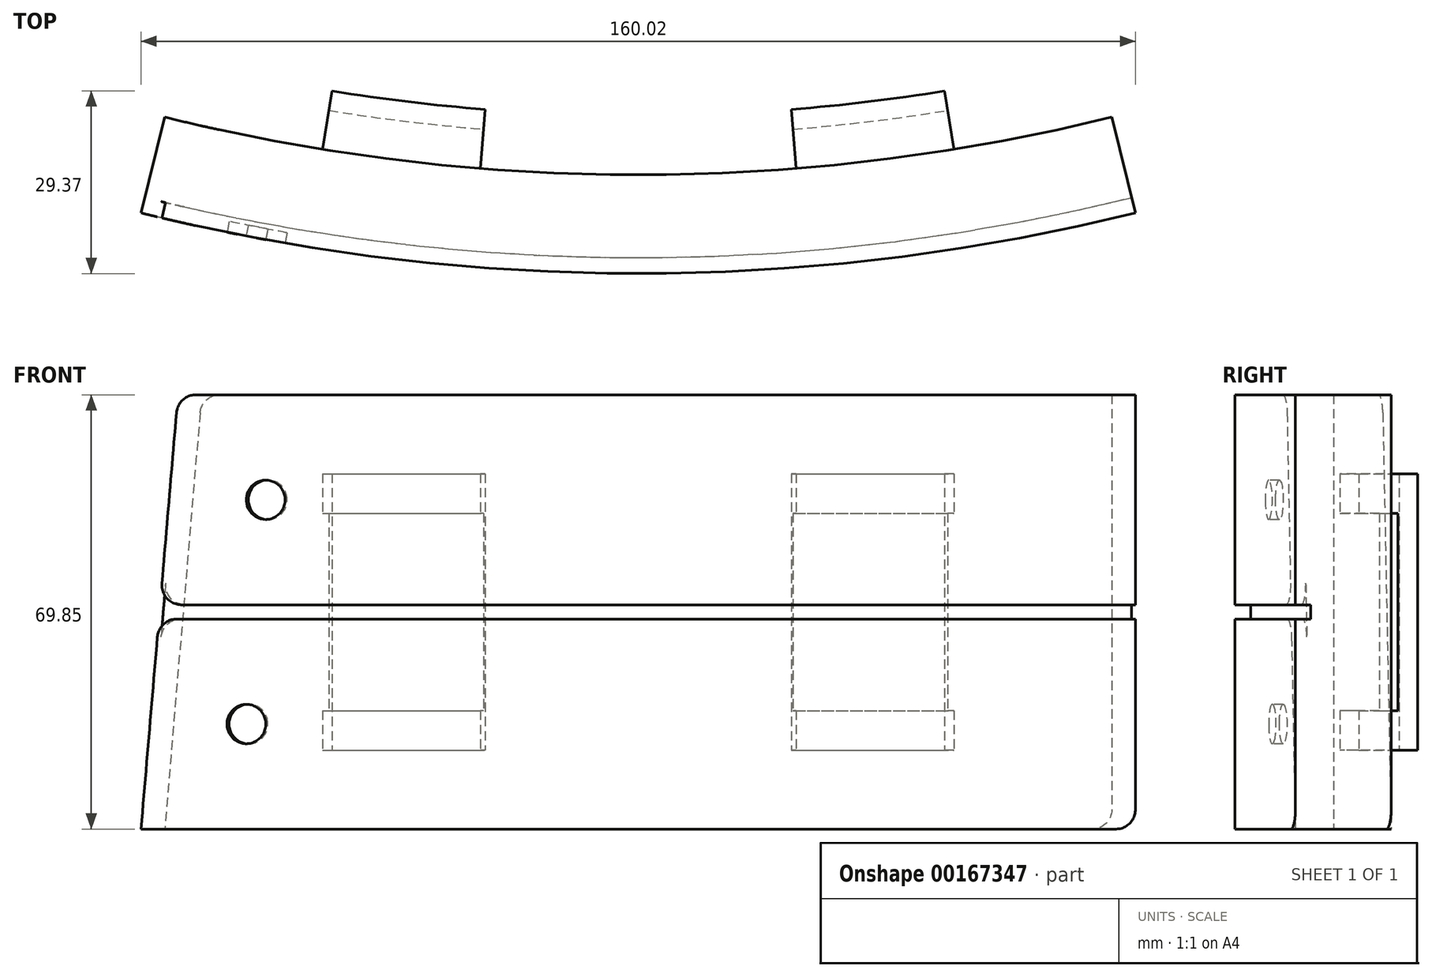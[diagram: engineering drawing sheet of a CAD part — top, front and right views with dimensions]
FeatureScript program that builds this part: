
annotation { "Feature Type Name" : "Feature", "Feature Type Description" : "" }
export const myFeature = defineFeature(function(context is Context, id is Id, definition is map)
    precondition{}
    {
        {
            var Q0;
            Q0=qCreatedBy(makeId("Top.planeOp"),FACE);
            var sketch = newSketch(context, id + "F0", { "sketchPlane" : qUnion([Q0])});
            skLineSegment(sketch, "E0.bottom", {"start": v(76.2, -22.11) * mm, "end": v(-76.2, -22.11) * mm, "construction": true});
            skLineSegment(sketch, "E0.top", {"start": v(76.2, 22.11) * mm, "end": v(-76.2, 22.11) * mm, "construction": true});
            skLineSegment(sketch, "E0.left", {"start": v(76.2, -22.11) * mm, "end": v(76.2, 22.11) * mm, "construction": true});
            skLineSegment(sketch, "E0.right", {"start": v(-76.2, -22.11) * mm, "end": v(-76.2, 22.11) * mm, "construction": true});
            skPoint(sketch, "E0.middle", {"position": v(0, 0) * mm});
            skLineSegment(sketch, "E1", {"start": v(0, 0) * mm, "end": v(0, 381.3) * mm, "construction": true});
            skArc(sketch, "E2", {"start": v(-76.2, -22.11) * mm, "mid": v(0, -31.4) * mm, "end": v(76.2, -22.11) * mm});
            skLineSegment(sketch, "E3", {"start": v(-76.2, -22.11) * mm, "end": v(0, 286.1) * mm, "construction": true});
            skLineSegment(sketch, "E4", {"start": v(76.2, -22.11) * mm, "end": v(0, 286.1) * mm, "construction": true});
            skArc(sketch, "E5", {"start": v(-80, -37.52) * mm, "mid": v(0, -47.27) * mm, "end": v(80, -37.52) * mm});
            skLineSegment(sketch, "E6", {"start": v(-76.2, -22.11) * mm, "end": v(-80, -37.52) * mm});
            skLineSegment(sketch, "E7", {"start": v(76.2, -22.11) * mm, "end": v(80, -37.52) * mm});
            skArc(sketch, "E8", {"start": v(-79.4, -35.06) * mm, "mid": v(0, -44.73) * mm, "end": v(79.4, -35.06) * mm});
            skSolve(sketch);
        }
        {
            var Q0;
            {var subQ0=sQuery(id+"F0.wireOp",EDGE,"E2");Q0=makeQuery(id+"F0.imprint","IMPRINT",FACE,{"disambiguationData":[TD([[makeQuery(id+"F0.imprint","IMPRINT",EDGE,{"derivedFrom":subQ0}),-1.0]])]});}
            var Q1;
            {var subQ0=sQuery(id+"F0.wireOp",EDGE,"E5");Q1=makeQuery(id+"F0.imprint","IMPRINT",FACE,{"disambiguationData":[TD([[makeQuery(id+"F0.imprint","IMPRINT",EDGE,{"derivedFrom":subQ0}),1.0]])]});}
            extrude(context, id + "F1", {"entities" : qUnion([Q0, Q1]), "depth" : 69.85 * mm});
        }
        {
            var Q0;
            {var subQ0=sQuery(id+"F0.wireOp",EDGE,"E5");Q0=makeQuery(id+"F0.imprint","IMPRINT",FACE,{"disambiguationData":[TD([[makeQuery(id+"F0.imprint","IMPRINT",EDGE,{"derivedFrom":subQ0}),1.0]])]});}
            extrude(context, id + "F2", {"entities" : qUnion([Q0]), "operationType" : NewBodyOperationType.REMOVE, "depth" : 36.07 * mm});
        }
        {
            var Q0;
            {var subQ0=sQuery(id+"F0.wireOp",EDGE,"E5");Q0=makeQuery(id+"F0.imprint","IMPRINT",FACE,{"disambiguationData":[TD([[makeQuery(id+"F0.imprint","IMPRINT",EDGE,{"derivedFrom":subQ0}),1.0]])]});}
            extrude(context, id + "F3", {"entities" : qUnion([Q0]), "operationType" : NewBodyOperationType.ADD, "depth" : 33.78 * mm});
        }
        {
            var Q0;
            Q0=sQuery(id+"F0.wireOp",EDGE,"E6");
            cPlane(context, id + "F4", {"entities" : qUnion([Q0]), "cplaneType" : CPlaneType.LINE_ANGLE, "offset" : 25.4 * mm, "angle" : 85 * degree, "width" : 152.4 * mm, "height" : 152.4 * mm});
        }
        {
            var Q0;
            Q0=qCreatedBy(id+"F4.planeOp",FACE);
            var sketch = newSketch(context, id + "F5", { "sketchPlane" : qUnion([Q0])});
            skLineSegment(sketch, "E9.bottom", {"start": v(-28.34, -23.6) * mm, "end": v(-88.35, -23.6) * mm});
            skLineSegment(sketch, "E9.top", {"start": v(-28.34, 74.53) * mm, "end": v(-88.35, 74.53) * mm});
            skLineSegment(sketch, "E9.left", {"start": v(-28.34, -23.6) * mm, "end": v(-28.34, 74.53) * mm});
            skLineSegment(sketch, "E9.right", {"start": v(-88.35, -23.6) * mm, "end": v(-88.35, 74.53) * mm});
            skSolve(sketch);
        }
        {
            var Q0;
            Q0 = qSketchRegion(id + "F5", true);
            extrude(context, id + "F6", {"entities" : qUnion([Q0]), "operationType" : NewBodyOperationType.REMOVE, "oppositeDirection" : true, "depth" : 25.4 * mm});
        }
        {
            var Q0;
            Q0=qCreatedBy(makeId("Top.planeOp"),FACE);
            var sketch = newSketch(context, id + "F7", { "sketchPlane" : qUnion([Q0])});
            skCircle(sketch, "E10", {"center": v(0, 286.1) * mm, "radius": 317.5 * mm});
            skLineSegment(sketch, "E11", {"start": v(-50.8, -27.3) * mm, "end": v(0, 286.1) * mm});
            skLineSegment(sketch, "E12", {"start": v(0, 286.1) * mm, "end": v(-25.4, -30.37) * mm});
            skLineSegment(sketch, "E13", {"start": v(25.4, -30.37) * mm, "end": v(0, 286.1) * mm});
            skLineSegment(sketch, "E14", {"start": v(50.8, -27.3) * mm, "end": v(0, 286.1) * mm});
            skArc(sketch, "E15", {"start": v(-49.28, -17.9) * mm, "mid": v(-36.99, -19.64) * mm, "end": v(-24.64, -20.88) * mm});
            skArc(sketch, "E16.trimOffspring", {"start": v(24.64, -20.88) * mm, "mid": v(36.99, -19.64) * mm, "end": v(49.28, -17.9) * mm});
            skArc(sketch, "E17", {"start": v(-49.78, -21.03) * mm, "mid": v(-37.37, -22.79) * mm, "end": v(-24.9, -24.04) * mm});
            skArc(sketch, "E18.trimOffspring", {"start": v(24.9, -24.04) * mm, "mid": v(37.37, -22.79) * mm, "end": v(49.78, -21.03) * mm});
            skSolve(sketch);
        }
        {
            var Q0;
            {var subQ5=sQuery(id+"F7.wireOp",EDGE,"E17");Q0=makeQuery(id+"F7.imprint","IMPRINT",FACE,{"disambiguationData":[TD([[makeQuery(id+"F7.imprint","IMPRINT",EDGE,{"derivedFrom":subQ5}),-1.0]])]});}
            var Q1;
            {var subQ0=sQuery(id+"F7.wireOp",EDGE,"E15");Q1=makeQuery(id+"F7.imprint","IMPRINT",FACE,{"disambiguationData":[TD([[makeQuery(id+"F7.imprint","IMPRINT",EDGE,{"derivedFrom":subQ0}),-1.0]])]});}
            var Q2;
            {var subQ5=sQuery(id+"F7.wireOp",EDGE,"E18.trimOffspring");Q2=makeQuery(id+"F7.imprint","IMPRINT",FACE,{"disambiguationData":[TD([[makeQuery(id+"F7.imprint","IMPRINT",EDGE,{"derivedFrom":subQ5}),-1.0]])]});}
            var Q3;
            {var subQ0=sQuery(id+"F7.wireOp",EDGE,"E16.trimOffspring");Q3=makeQuery(id+"F7.imprint","IMPRINT",FACE,{"disambiguationData":[TD([[makeQuery(id+"F7.imprint","IMPRINT",EDGE,{"derivedFrom":subQ0}),-1.0]])]});}
            extrude(context, id + "F8", {"entities" : qUnion([Q0, Q1, Q2, Q3]), "operationType" : NewBodyOperationType.ADD, "depth" : 57.15 * mm});
        }
        {
            var Q0;
            {var subQ5=sQuery(id+"F7.wireOp",EDGE,"E18.trimOffspring");Q0=makeQuery(id+"F7.imprint","IMPRINT",FACE,{"disambiguationData":[TD([[makeQuery(id+"F7.imprint","IMPRINT",EDGE,{"derivedFrom":subQ5}),-1.0]])]});}
            var Q1;
            {var subQ5=sQuery(id+"F7.wireOp",EDGE,"E17");Q1=makeQuery(id+"F7.imprint","IMPRINT",FACE,{"disambiguationData":[TD([[makeQuery(id+"F7.imprint","IMPRINT",EDGE,{"derivedFrom":subQ5}),-1.0]])]});}
            extrude(context, id + "F9", {"entities" : qUnion([Q0, Q1]), "operationType" : NewBodyOperationType.REMOVE, "depth" : 50.8 * mm});
        }
        {
            var Q0;
            {var subQ5=sQuery(id+"F7.wireOp",EDGE,"E18.trimOffspring");Q0=makeQuery(id+"F7.imprint","IMPRINT",FACE,{"disambiguationData":[TD([[makeQuery(id+"F7.imprint","IMPRINT",EDGE,{"derivedFrom":subQ5}),-1.0]])]});}
            var Q1;
            {var subQ5=sQuery(id+"F7.wireOp",EDGE,"E17");Q1=makeQuery(id+"F7.imprint","IMPRINT",FACE,{"disambiguationData":[TD([[makeQuery(id+"F7.imprint","IMPRINT",EDGE,{"derivedFrom":subQ5}),-1.0]])]});}
            extrude(context, id + "F10", {"entities" : qUnion([Q0, Q1]), "operationType" : NewBodyOperationType.ADD, "depth" : 19.05 * mm});
        }
        {
            var Q0;
            {var subQ5=sQuery(id+"F7.wireOp",EDGE,"E18.trimOffspring");Q0=makeQuery(id+"F7.imprint","IMPRINT",FACE,{"disambiguationData":[TD([[makeQuery(id+"F7.imprint","IMPRINT",EDGE,{"derivedFrom":subQ5}),-1.0]])]});}
            var Q1;
            {var subQ0=sQuery(id+"F7.wireOp",EDGE,"E16.trimOffspring");Q1=makeQuery(id+"F7.imprint","IMPRINT",FACE,{"disambiguationData":[TD([[makeQuery(id+"F7.imprint","IMPRINT",EDGE,{"derivedFrom":subQ0}),-1.0]])]});}
            var Q2;
            {var subQ5=sQuery(id+"F7.wireOp",EDGE,"E17");Q2=makeQuery(id+"F7.imprint","IMPRINT",FACE,{"disambiguationData":[TD([[makeQuery(id+"F7.imprint","IMPRINT",EDGE,{"derivedFrom":subQ5}),-1.0]])]});}
            var Q3;
            {var subQ0=sQuery(id+"F7.wireOp",EDGE,"E15");Q3=makeQuery(id+"F7.imprint","IMPRINT",FACE,{"disambiguationData":[TD([[makeQuery(id+"F7.imprint","IMPRINT",EDGE,{"derivedFrom":subQ0}),-1.0]])]});}
            extrude(context, id + "F11", {"entities" : qUnion([Q0, Q1, Q2, Q3]), "operationType" : NewBodyOperationType.REMOVE, "depth" : 12.7 * mm});
        }
        {
            var Q0;
            Q0=qCreatedBy(makeId("Top.planeOp"),FACE);
            var sketch = newSketch(context, id + "F12", { "sketchPlane" : qUnion([Q0])});
            skCircle(sketch, "E19", {"center": v(0, 286.1) * mm, "radius": 333.38 * mm});
            skLineSegment(sketch, "E20", {"start": v(0, 286.1) * mm, "end": v(-64.51, -40.96) * mm});
            skSolve(sketch);
        }
        {
            var Q0;
            Q0=sQuery(id+"F12.wireOp",VERTEX,"E20.end");
            var Q1;
            Q1=sQuery(id+"F12.wireOp",EDGE,"E20");
            cPlane(context, id + "F13", {"entities" : qUnion([Q0, Q1]), "cplaneType" : CPlaneType.LINE_POINT, "offset" : 25.4 * mm, "width" : 152.4 * mm, "height" : 152.4 * mm});
        }
        {
            var Q0;
            Q0=qCreatedBy(id+"F13.planeOp",FACE);
            var sketch = newSketch(context, id + "F14", { "sketchPlane" : qUnion([Q0])});
            skLineSegment(sketch, "E21", {"start": v(-55.37, 0) * mm, "end": v(-49.8, 63.7) * mm, "construction": true});
            skLineSegment(sketch, "E22", {"start": v(-55.37, 0) * mm, "end": v(-31.2, 0) * mm, "construction": true});
            skCircle(sketch, "E23", {"center": v(-53.89, 16.9) * mm, "radius": 3.18 * mm});
            skCircle(sketch, "E24", {"center": v(-50.73, 52.96) * mm, "radius": 3.18 * mm});
            skSolve(sketch);
        }
        {
            var Q0;
            Q0=makeQuery(id+"F14.imprint","IMPRINT",FACE,{"disambiguationData":[TD([[makeQuery(id+"F14.imprint","IMPRINT",EDGE,{"derivedFrom":sQuery(id+"F14.wireOp",EDGE,"E24")}),1.0]])]});
            var Q1;
            Q1=makeQuery(id+"F14.imprint","IMPRINT",FACE,{"disambiguationData":[TD([[makeQuery(id+"F14.imprint","IMPRINT",EDGE,{"derivedFrom":sQuery(id+"F14.wireOp",EDGE,"E23")}),1.0]])]});
            extrude(context, id + "F15", {"entities" : qUnion([Q0, Q1]), "operationType" : NewBodyOperationType.REMOVE, "oppositeDirection" : true, "depth" : 1.78 * mm});
        }
        {
            var Q0;
            Q0=makeQuery(id+"F6.boolean.opBoolean","INTERSECT",EDGE,{"derivedFrom":[makeQuery(id+"F1.opExtrude","CAP_FACE",FACE,{"disambiguationData":[OSD([sQuery(id+"F0.wireOp",EDGE,"E2"),sQuery(id+"F0.wireOp",EDGE,"E5"),sQuery(id+"F0.wireOp",EDGE,"E6"),sQuery(id+"F0.wireOp",EDGE,"E7")])],"isStart":false}),makeQuery(id+"F6.opExtrude","CAP_FACE",FACE,{"disambiguationData":[OSD([sQuery(id+"F5.wireOp",EDGE,"E9.bottom"),sQuery(id+"F5.wireOp",EDGE,"E9.top"),sQuery(id+"F5.wireOp",EDGE,"E9.left"),sQuery(id+"F5.wireOp",EDGE,"E9.right")])],"isStart":true})]});
            var Q1;
            {var subQ0=sQuery(id+"F0.wireOp",EDGE,"E6");Q1=makeQuery(id+"F3.boolean.opBoolean","MERGE",EDGE,{"derivedFrom":[makeQuery(id+"F1.opExtrude","CAP_EDGE",EDGE,{"disambiguationData":[OSD([subQ0])],"isStart":true}),makeQuery(id+"F3.opExtrude","CAP_EDGE",EDGE,{"disambiguationData":[OSD([subQ0])],"isStart":true})]});}
            var Q2;
            Q2=makeQuery(id+"FK32j8JhmoBZqBw_1.1.F6.boolean.opBoolean","INTERSECT",EDGE,{"derivedFrom":[makeQuery(id+"F1.opExtrude","CAP_FACE",FACE,{"disambiguationData":[OSD([sQuery(id+"F0.wireOp",EDGE,"E2"),sQuery(id+"F0.wireOp",EDGE,"E5"),sQuery(id+"F0.wireOp",EDGE,"E6"),sQuery(id+"F0.wireOp",EDGE,"E7")])],"isStart":false}),makeQuery(id+"FK32j8JhmoBZqBw_1.1.F6.opExtrude","CAP_FACE",FACE,{"disambiguationData":[OSD([sQuery(id+"F5.wireOp",EDGE,"E9.bottom"),sQuery(id+"F5.wireOp",EDGE,"E9.top"),sQuery(id+"F5.wireOp",EDGE,"E9.left"),sQuery(id+"F5.wireOp",EDGE,"E9.right")])],"isStart":true})]});
            var Q3;
            {var subQ0=sQuery(id+"F0.wireOp",EDGE,"E7");Q3=makeQuery(id+"F3.boolean.opBoolean","MERGE",EDGE,{"derivedFrom":[makeQuery(id+"F1.opExtrude","CAP_EDGE",EDGE,{"disambiguationData":[OSD([subQ0])],"isStart":true}),makeQuery(id+"F3.opExtrude","CAP_EDGE",EDGE,{"disambiguationData":[OSD([subQ0])],"isStart":true})]});}
            var Q4;
            Q4=makeQuery(id+"F6.boolean.opBoolean","INTERSECT",EDGE,{"derivedFrom":[makeQuery(id+"F2.boolean.opBoolean","COPY",FACE,{"derivedFrom":makeQuery(id+"F2.opExtrude","CAP_FACE",FACE,{"disambiguationData":[OSD([sQuery(id+"F0.wireOp",EDGE,"E5"),sQuery(id+"F0.wireOp",EDGE,"E6"),sQuery(id+"F0.wireOp",EDGE,"E7"),sQuery(id+"F0.wireOp",EDGE,"E8")])],"isStart":false})}),makeQuery(id+"F6.opExtrude","CAP_FACE",FACE,{"disambiguationData":[OSD([sQuery(id+"F5.wireOp",EDGE,"E9.bottom"),sQuery(id+"F5.wireOp",EDGE,"E9.top"),sQuery(id+"F5.wireOp",EDGE,"E9.left"),sQuery(id+"F5.wireOp",EDGE,"E9.right")])],"isStart":true})]});
            var Q5;
            Q5=makeQuery(id+"F6.boolean.opBoolean","INTERSECT",EDGE,{"derivedFrom":[makeQuery(id+"F3.opExtrude","CAP_FACE",FACE,{"disambiguationData":[OSD([sQuery(id+"F0.wireOp",EDGE,"E5"),sQuery(id+"F0.wireOp",EDGE,"E6"),sQuery(id+"F0.wireOp",EDGE,"E7"),sQuery(id+"F0.wireOp",EDGE,"E8")])],"isStart":false}),makeQuery(id+"F6.opExtrude","CAP_FACE",FACE,{"disambiguationData":[OSD([sQuery(id+"F5.wireOp",EDGE,"E9.bottom"),sQuery(id+"F5.wireOp",EDGE,"E9.top"),sQuery(id+"F5.wireOp",EDGE,"E9.left"),sQuery(id+"F5.wireOp",EDGE,"E9.right")])],"isStart":true})]});
            var Q6;
            Q6=makeQuery(id+"FK32j8JhmoBZqBw_1.1.F6.boolean.opBoolean","INTERSECT",EDGE,{"derivedFrom":[makeQuery(id+"F2.boolean.opBoolean","COPY",FACE,{"derivedFrom":makeQuery(id+"F2.opExtrude","CAP_FACE",FACE,{"disambiguationData":[OSD([sQuery(id+"F0.wireOp",EDGE,"E5"),sQuery(id+"F0.wireOp",EDGE,"E6"),sQuery(id+"F0.wireOp",EDGE,"E7"),sQuery(id+"F0.wireOp",EDGE,"E8")])],"isStart":false})}),makeQuery(id+"FK32j8JhmoBZqBw_1.1.F6.opExtrude","CAP_FACE",FACE,{"disambiguationData":[OSD([sQuery(id+"F5.wireOp",EDGE,"E9.bottom"),sQuery(id+"F5.wireOp",EDGE,"E9.top"),sQuery(id+"F5.wireOp",EDGE,"E9.left"),sQuery(id+"F5.wireOp",EDGE,"E9.right")])],"isStart":true})]});
            var Q7;
            Q7=makeQuery(id+"FK32j8JhmoBZqBw_1.1.F6.boolean.opBoolean","INTERSECT",EDGE,{"derivedFrom":[makeQuery(id+"F3.opExtrude","CAP_FACE",FACE,{"disambiguationData":[OSD([sQuery(id+"F0.wireOp",EDGE,"E5"),sQuery(id+"F0.wireOp",EDGE,"E6"),sQuery(id+"F0.wireOp",EDGE,"E7"),sQuery(id+"F0.wireOp",EDGE,"E8")])],"isStart":false}),makeQuery(id+"FK32j8JhmoBZqBw_1.1.F6.opExtrude","CAP_FACE",FACE,{"disambiguationData":[OSD([sQuery(id+"F5.wireOp",EDGE,"E9.bottom"),sQuery(id+"F5.wireOp",EDGE,"E9.top"),sQuery(id+"F5.wireOp",EDGE,"E9.left"),sQuery(id+"F5.wireOp",EDGE,"E9.right")])],"isStart":true})]});
            fillet(context, id + "F16", {"entities" : qUnion([Q0, Q1, Q2, Q3, Q4, Q5, Q6, Q7]), "radius" : 3.17 * mm, "tangentPropagation" : true, "allowEdgeOverflow" : false});
        }
    });
